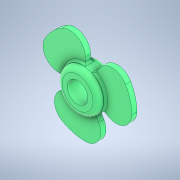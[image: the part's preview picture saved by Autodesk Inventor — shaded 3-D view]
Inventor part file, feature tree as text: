
AUTODESK INVENTOR PART (.ipt)
format: ipt  version: 2021 (Build 250183000, 183)  size: 219,648 bytes
history: native  units: mm
features: sketch x3, fillet x3, extrude x1, revolve x1, pattern_circular x1
ambient origin geometry x8: Origin, YZ Plane, XZ Plane, XY Plane, X Axis, Y Axis, Z Axis, Center Point
bodies: Solid1 (feature_tree)
feature tree (9):
  extrude  "Extrusion1"  Depth=2.0mm
  sketch  "Sketch2"  dims[d2=2.0mm d3=0.0mm d4=0.5mm d5=2.5mm d6=0.75mm]
  revolve  "Revolution1"  [1 undecoded]
  fillet  "Fillet1"  Radius=2.5mm
  fillet  "Fillet2"  Radius=0.75mm
  pattern_circular  "Circular Pattern1"  [2 undecoded]
  fillet  "Fillet3"  Radius=0.2mm
  sketch  "Sketch1"  dims[d0=4.0mm d1=2.0mm]
  sketch  "Sketch3"  dims[d7=90.0deg d8=1.5mm d9=0.2mm d10=30.0mm d11=360.0deg d13=0.5mm d14=0.5mm d15=4.0mm]
note: 3 required parameter values undecoded (feature->parameter linkage not recoverable at this tier; creation-order binding heuristic only, values carry confidence <= 0.55)